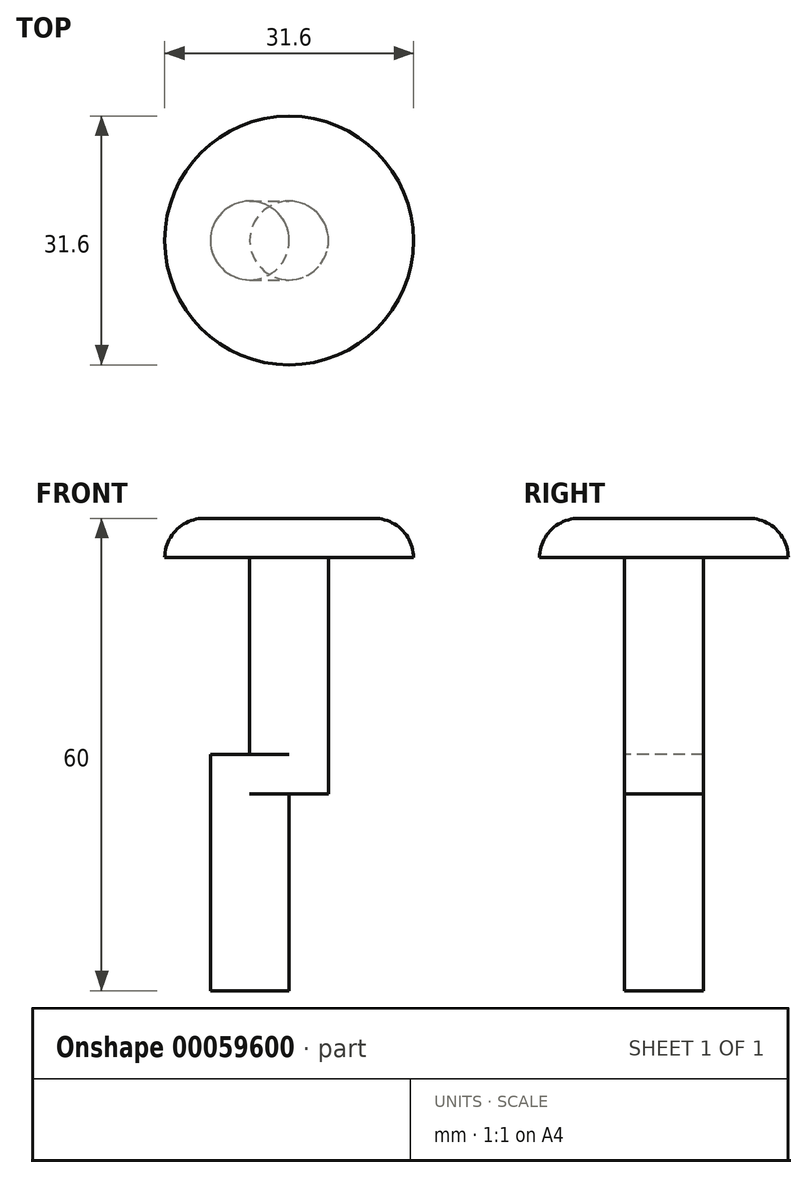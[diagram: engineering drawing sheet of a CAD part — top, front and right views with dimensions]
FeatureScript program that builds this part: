
annotation { "Feature Type Name" : "Feature", "Feature Type Description" : "" }
export const myFeature = defineFeature(function(context is Context, id is Id, definition is map)
    precondition{}
    {
        {
            var Q0;
            Q0=qCreatedBy(makeId("Top.planeOp"),FACE);
            var sketch = newSketch(context, id + "F0", { "sketchPlane" : qUnion([Q0])});
            skCircle(sketch, "E0", {"center": v(0, 0) * mm, "radius": 5 * mm});
            skSolve(sketch);
        }
        {
            var Q0;
            Q0 = qSketchRegion(id + "F0", true);
            extrude(context, id + "F1", {"entities" : qUnion([Q0]), "depth" : 25 * mm});
        }
        {
            var Q0;
            Q0=makeQuery(id+"F1.opExtrude","CAP_FACE",FACE,{"disambiguationData":[OSD([sQuery(id+"F0.wireOp",EDGE,"E0")])],"isStart":false});
            var sketch = newSketch(context, id + "F2", { "sketchPlane" : qUnion([Q0])});
            skLineSegment(sketch, "E1.bottom", {"start": v(-5, 5) * mm, "end": v(10, 5) * mm});
            skLineSegment(sketch, "E1.top", {"start": v(-5, -5) * mm, "end": v(10, -5) * mm});
            skLineSegment(sketch, "E1.left", {"start": v(-5, 5) * mm, "end": v(-5, -5) * mm});
            skLineSegment(sketch, "E1.right", {"start": v(10, 5) * mm, "end": v(10, -5) * mm});
            skSolve(sketch);
        }
        {
            var Q0;
            Q0 = qSketchRegion(id + "F2", true);
            extrude(context, id + "F3", {"entities" : qUnion([Q0]), "operationType" : NewBodyOperationType.ADD, "depth" : 5 * mm});
        }
        {
            var Q0;
            Q0=makeQuery(id+"F3.opExtrude","CAP_FACE",FACE,{"disambiguationData":[OSD([sQuery(id+"F2.wireOp",EDGE,"E1.bottom"),sQuery(id+"F2.wireOp",EDGE,"E1.top"),sQuery(id+"F2.wireOp",EDGE,"E1.left"),sQuery(id+"F2.wireOp",EDGE,"E1.right")])],"isStart":false});
            var sketch = newSketch(context, id + "F4", { "sketchPlane" : qUnion([Q0])});
            skCircle(sketch, "E2", {"center": v(5, 0) * mm, "radius": 5 * mm});
            skSolve(sketch);
        }
        {
            var Q0;
            Q0 = qSketchRegion(id + "F4", true);
            extrude(context, id + "F5", {"entities" : qUnion([Q0]), "operationType" : NewBodyOperationType.ADD, "depth" : 25 * mm});
        }
        {
            var Q0;
            Q0=makeQuery(id+"F3.opExtrude","SWEPT_EDGE",EDGE,{"disambiguationData":[OSD([sQuery(id+"F2.wireOp",EDGE,"E1.top"),sQuery(id+"F2.wireOp",EDGE,"E1.right")])]});
            var Q1;
            Q1=makeQuery(id+"F3.opExtrude","SWEPT_EDGE",EDGE,{"disambiguationData":[OSD([sQuery(id+"F2.wireOp",EDGE,"E1.bottom"),sQuery(id+"F2.wireOp",EDGE,"E1.right")])]});
            var Q2;
            Q2=makeQuery(id+"F3.opExtrude","SWEPT_EDGE",EDGE,{"disambiguationData":[OSD([sQuery(id+"F2.wireOp",EDGE,"E1.bottom"),sQuery(id+"F2.wireOp",EDGE,"E1.left")])]});
            var Q3;
            Q3=makeQuery(id+"F3.opExtrude","SWEPT_EDGE",EDGE,{"disambiguationData":[OSD([sQuery(id+"F2.wireOp",EDGE,"E1.top"),sQuery(id+"F2.wireOp",EDGE,"E1.left")])]});
            fillet(context, id + "F6", {"entities" : qUnion([Q0, Q1, Q2, Q3]), "radius" : 5 * mm, "tangentPropagation" : true, "allowEdgeOverflow" : false});
        }
        {
            var Q0;
            Q0=makeQuery(id+"F5.opExtrude","CAP_FACE",FACE,{"disambiguationData":[OSD([sQuery(id+"F4.wireOp",EDGE,"E2")])],"isStart":false});
            var sketch = newSketch(context, id + "F7", { "sketchPlane" : qUnion([Q0])});
            skCircle(sketch, "E3", {"center": v(5, 0) * mm, "radius": 15.8 * mm});
            skSolve(sketch);
        }
        {
            var Q0;
            Q0 = qSketchRegion(id + "F7", true);
            extrude(context, id + "F8", {"entities" : qUnion([Q0]), "operationType" : NewBodyOperationType.ADD, "depth" : 5 * mm});
        }
        {
            var Q0;
            Q0=makeQuery(id+"F8.opExtrude","CAP_FACE",FACE,{"disambiguationData":[OSD([sQuery(id+"F7.wireOp",EDGE,"E3")])],"isStart":false});
            fillet(context, id + "F9", {"entities" : qUnion([Q0]), "radius" : 5 * mm, "tangentPropagation" : true, "allowEdgeOverflow" : false});
        }
    });
